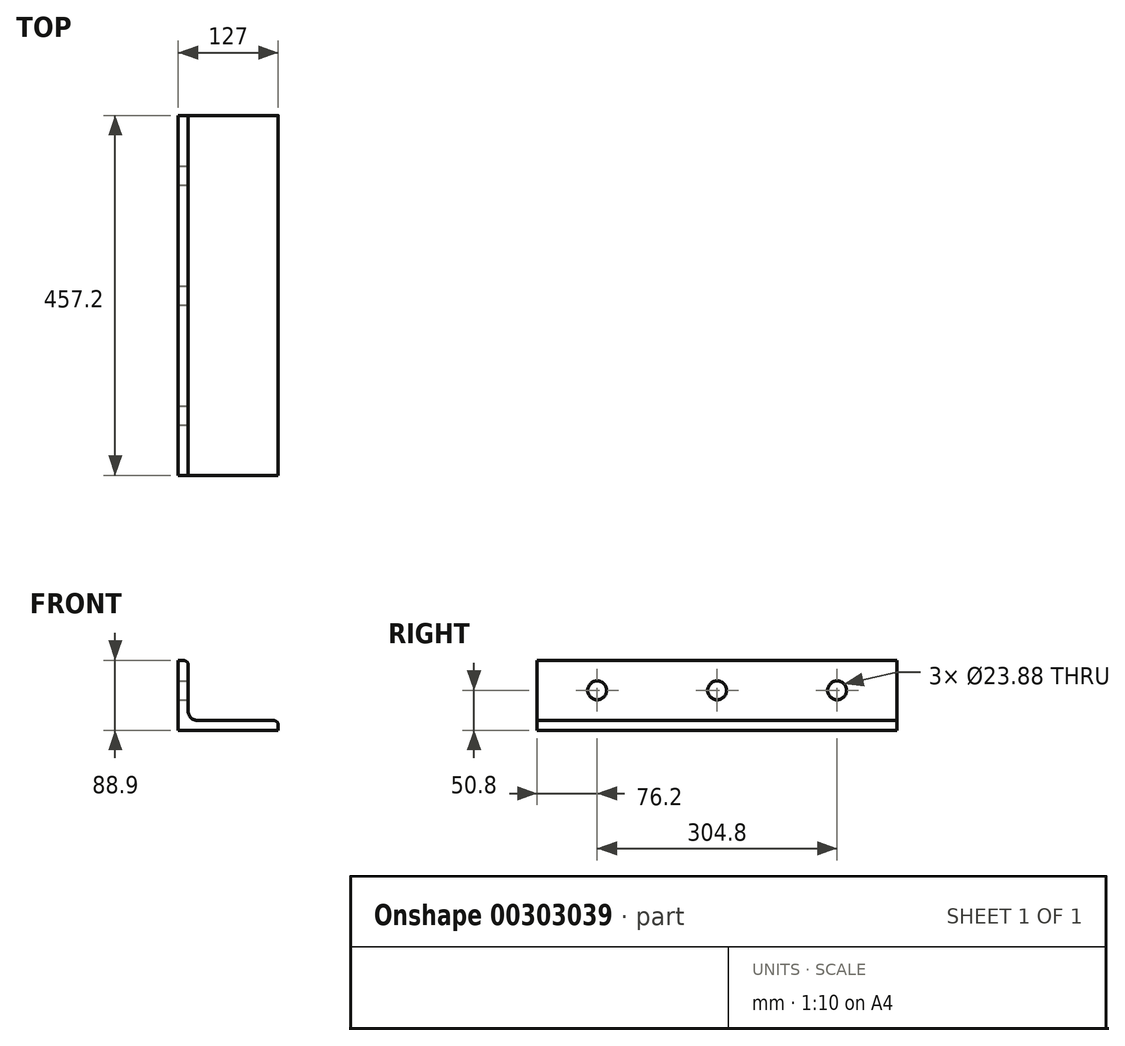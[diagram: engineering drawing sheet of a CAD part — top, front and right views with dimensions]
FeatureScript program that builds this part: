
annotation { "Feature Type Name" : "Feature", "Feature Type Description" : "" }
export const myFeature = defineFeature(function(context is Context, id is Id, definition is map)
    precondition{}
    {
        {
            var Q0;
            Q0=qCreatedBy(makeId("Front.planeOp"),FACE);
            var sketch = newSketch(context, id + "F0", { "sketchPlane" : qUnion([Q0])});
            skLineSegment(sketch, "E0.0.0", {"start": v(0, 88.9) * mm, "end": v(0, 0) * mm});
            skLineSegment(sketch, "E0.0.1", {"start": v(0, 0) * mm, "end": v(127, 0) * mm});
            skLineSegment(sketch, "E0.0.2", {"start": v(127, 0) * mm, "end": v(127, 6.35) * mm});
            skArc(sketch, "E0.0.3", {"start": v(127, 6.35) * mm, "mid": v(125.14, 10.84) * mm, "end": v(120.65, 12.7) * mm});
            skLineSegment(sketch, "E0.0.4", {"start": v(120.65, 12.7) * mm, "end": v(23.81, 12.7) * mm});
            skArc(sketch, "E0.0.5", {"start": v(23.81, 12.7) * mm, "mid": v(15.95, 15.95) * mm, "end": v(12.7, 23.81) * mm});
            skLineSegment(sketch, "E0.0.6", {"start": v(12.7, 23.81) * mm, "end": v(12.7, 82.55) * mm});
            skArc(sketch, "E0.0.7", {"start": v(12.7, 82.55) * mm, "mid": v(10.84, 87.04) * mm, "end": v(6.35, 88.9) * mm});
            skLineSegment(sketch, "E0.0.8", {"start": v(6.35, 88.9) * mm, "end": v(0, 88.9) * mm});
            skSolve(sketch);
        }
        {
            var Q0;
            Q0=makeQuery(id+"F0.imprint","IMPRINT",FACE,{"disambiguationData":[TD([[makeQuery(id+"F0.imprint","IMPRINT",EDGE,{"derivedFrom":sQuery(id+"F0.wireOp",EDGE,"E0.0.0")}),1.0]])]});
            extrude(context, id + "F1", {"entities" : qUnion([Q0]), "depth" : 457.2 * mm, "symmetric" : true});
        }
        {
            var Q0;
            Q0=qCreatedBy(makeId("Right.planeOp"),FACE);
            var sketch = newSketch(context, id + "F2", { "sketchPlane" : qUnion([Q0])});
            skLineSegment(sketch, "E1", {"start": v(-177.21, 50.8) * mm, "end": v(176.63, 50.8) * mm, "construction": true});
            skPoint(sketch, "E2", {"position": v(-152.4, 50.8) * mm});
            skPoint(sketch, "E3", {"position": v(152.4, 50.8) * mm});
            skPoint(sketch, "E4", {"position": v(0, 50.8) * mm});
            skSolve(sketch);
        }
        {
            var Q0;
            Q0=sQuery(id+"F2.wireOp",VERTEX,"E2");
            var Q1;
            Q1=sQuery(id+"F2.wireOp",VERTEX,"E4");
            var Q2;
            Q2=sQuery(id+"F2.wireOp",VERTEX,"E3");
            var Q3;
            Q3=makeQuery(id+"F1.opExtrude","SWEPT_BODY",BODY,{"disambiguationData":[OSD([sQuery(id+"F0.wireOp",EDGE,"E0.0.0"),sQuery(id+"F0.wireOp",EDGE,"E0.0.1"),sQuery(id+"F0.wireOp",EDGE,"E0.0.2"),sQuery(id+"F0.wireOp",EDGE,"E0.0.3"),sQuery(id+"F0.wireOp",EDGE,"E0.0.4"),sQuery(id+"F0.wireOp",EDGE,"E0.0.5"),sQuery(id+"F0.wireOp",EDGE,"E0.0.6"),sQuery(id+"F0.wireOp",EDGE,"E0.0.7"),sQuery(id+"F0.wireOp",EDGE,"E0.0.8")])]});
            hole(context, id + "F3", {"style" : HoleStyle.SIMPLE, "endStyle" : HoleEndStyle.THROUGH, "oppositeDirection" : true, "holeDiameter" : 23.88 * mm, "tappedDepth" : 12.7 * mm, "tapClearance" : 3, "locations" : qUnion([Q0, Q1, Q2]), "scope" : qUnion([Q3])});
        }
    });
